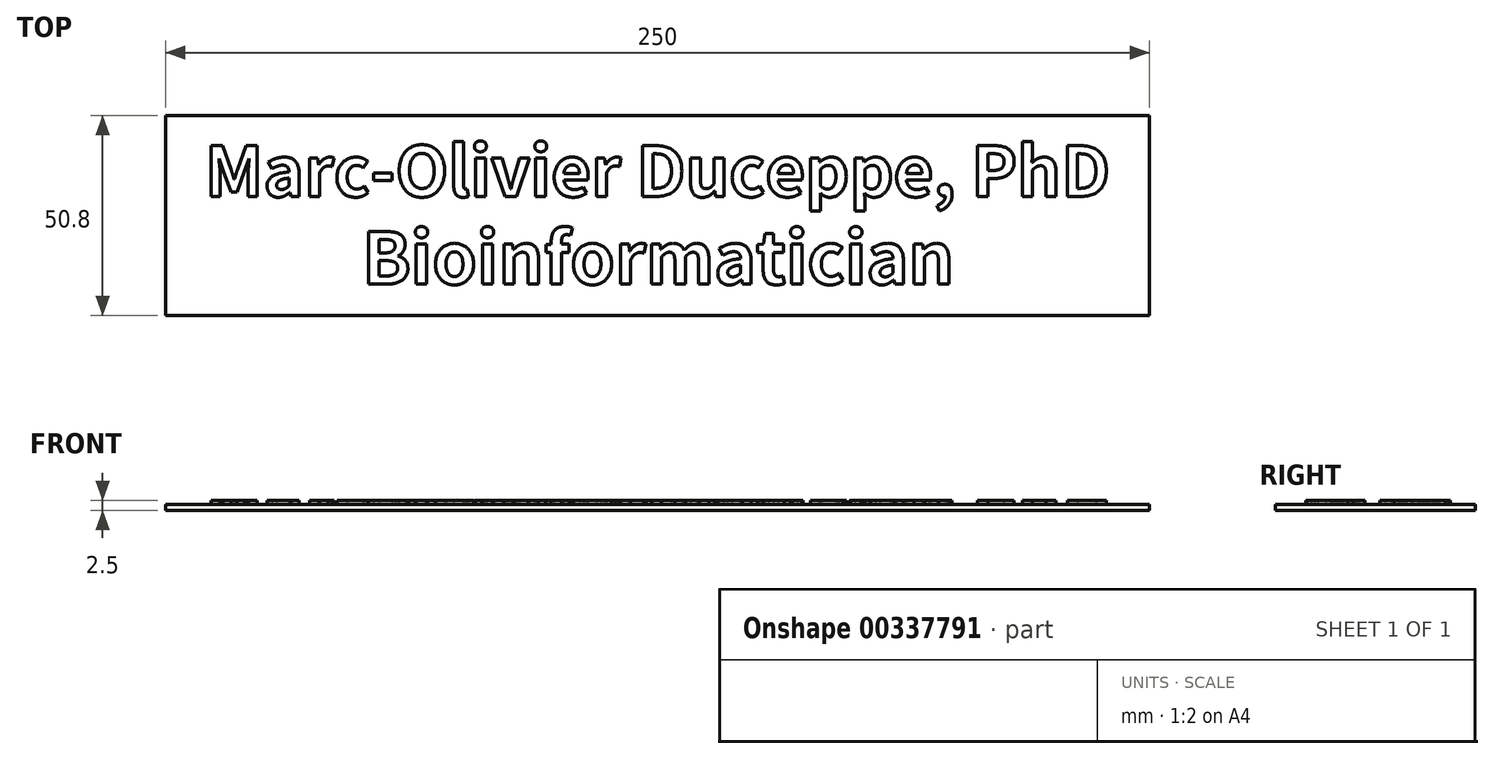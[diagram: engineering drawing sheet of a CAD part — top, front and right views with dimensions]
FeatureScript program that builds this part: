
annotation { "Feature Type Name" : "Feature", "Feature Type Description" : "" }
export const myFeature = defineFeature(function(context is Context, id is Id, definition is map)
    precondition{}
    {
        {
            var Q0;
            Q0=qCreatedBy(makeId("Top.planeOp"),FACE);
            var sketch = newSketch(context, id + "F0", { "sketchPlane" : qUnion([Q0])});
            skLineSegment(sketch, "E0.bottom", {"start": v(125, -25.4) * mm, "end": v(-125, -25.4) * mm});
            skLineSegment(sketch, "E0.top", {"start": v(125, 25.4) * mm, "end": v(-125, 25.4) * mm});
            skLineSegment(sketch, "E0.left", {"start": v(125, -25.4) * mm, "end": v(125, 25.4) * mm});
            skLineSegment(sketch, "E0.right", {"start": v(-125, -25.4) * mm, "end": v(-125, 25.4) * mm});
            skPoint(sketch, "E0.middle", {"position": v(0, 0) * mm});
            skSolve(sketch);
        }
        {
            var Q0;
            Q0 = qSketchRegion(id + "F0", true);
            extrude(context, id + "F1", {"entities" : qUnion([Q0]), "depth" : 1.5 * mm});
        }
        {
            var Q0;
            Q0=makeQuery(id+"F1.opExtrude","CAP_FACE",FACE,{"disambiguationData":[OSD([sQuery(id+"F0.wireOp",EDGE,"E0.bottom"),sQuery(id+"F0.wireOp",EDGE,"E0.top"),sQuery(id+"F0.wireOp",EDGE,"E0.left"),sQuery(id+"F0.wireOp",EDGE,"E0.right")])],"isStart":false});
            var sketch = newSketch(context, id + "F2", { "sketchPlane" : qUnion([Q0])});
            skText(sketch, "E1", { "text": "Marc-Olivier Duceppe, PhD", "fontName": "NotoSansCJKsc-Bold.otf"});
            skText(sketch, "E2", { "text": "Bioinformatician", "fontName": "NotoSansCJKsc-Bold.otf"});
            const initialGuessF2  = {"E1": [-0.115, 0.00485, 1, 0, 0.01255], "E2": [-0.075, -0.0174, 1, 0, 0.01299]};
            skSetInitialGuess(sketch, initialGuessF2);
            skSolve(sketch);
        }
        {
            var Q0;
            Q0 = qSketchRegion(id + "F2", true);
            extrude(context, id + "F3", {"entities" : qUnion([Q0]), "operationType" : NewBodyOperationType.ADD, "depth" : 1 * mm});
        }
    });
